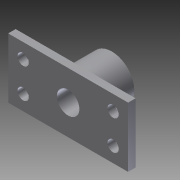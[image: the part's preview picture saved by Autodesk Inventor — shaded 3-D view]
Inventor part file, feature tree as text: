
AUTODESK INVENTOR PART (.ipt)
format: ipt  version: 2011 (Build 150239000, 239)  size: 100,352 bytes
history: native  units: in
note: dims shown in document units (in); Inventor stores cm internally (conversion verified against a paired STEP export)
features: sketch x4, extrude x3, hole x1
ambient origin geometry x8: Origin, YZ Plane, XZ Plane, XY Plane, X Axis, Y Axis, Z Axis, Center Point
bodies: Solid1 (feature_tree)
feature tree (8):
  extrude  "Extrusion1"  Depth=0.3022in TaperAngle=0.0deg
  extrude  "Extrusion2"  Depth=0.3022in TaperAngle=0.0deg
  extrude  "Extrusion3"  Depth=0.5in
  hole  "Hole1"  [1 undecoded]
  sketch  "Sketch1"  dims[d0=0.374in d1=0.3022in d2=0.0in]
  sketch  "Sketch2"  dims[d3=0.1875in d4=0.3022in d5=0.0in]
  sketch  "Sketch3"  dims[d6=1.0in d7=0.5in]
  sketch  "Sketch4"  dims[d8=0.0625in d9=0.0in d10=0.094in d11=0.75in d12=0.375in d13=0.25in d14=0.5635in d15=1.0in d16=0.8108in]
note: 1 required parameter value undecoded (feature->parameter linkage not recoverable at this tier; creation-order binding heuristic only, values carry confidence <= 0.55)
